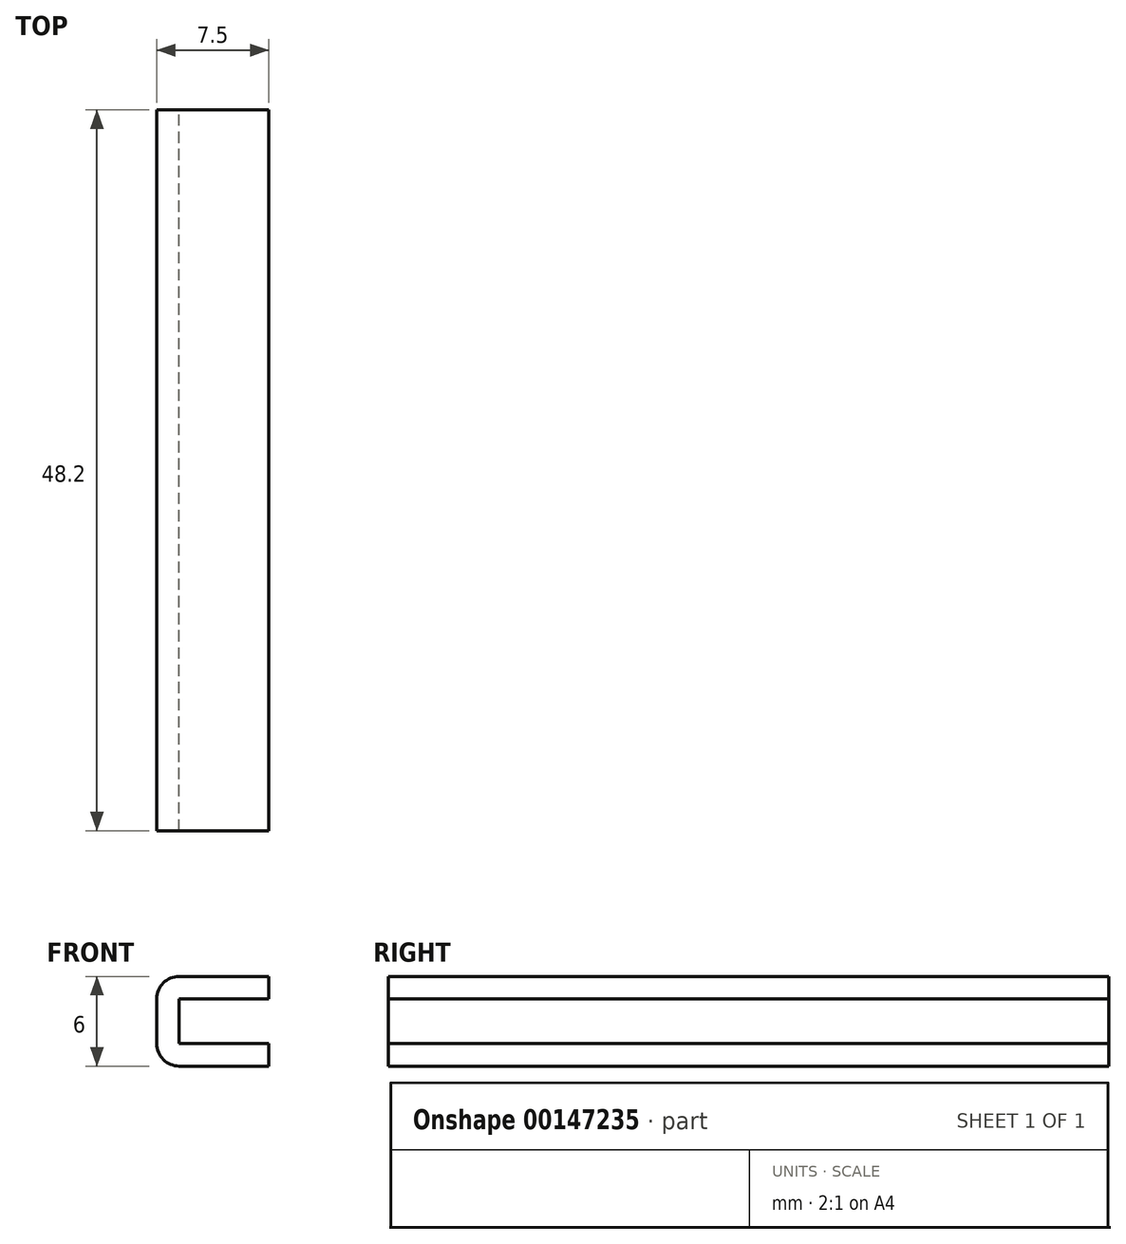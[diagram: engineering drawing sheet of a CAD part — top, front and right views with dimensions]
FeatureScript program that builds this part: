
annotation { "Feature Type Name" : "Feature", "Feature Type Description" : "" }
export const myFeature = defineFeature(function(context is Context, id is Id, definition is map)
    precondition{}
    {
        {
            var Q0;
            Q0=qCreatedBy(makeId("Front.planeOp"),FACE);
            var sketch = newSketch(context, id + "F0", { "sketchPlane" : qUnion([Q0])});
            skLineSegment(sketch, "E0", {"start": v(6, 1.5) * mm, "end": v(0, 1.5) * mm});
            skLineSegment(sketch, "E1", {"start": v(0, 1.5) * mm, "end": v(0, -1.5) * mm});
            skLineSegment(sketch, "E2", {"start": v(0, -1.5) * mm, "end": v(6, -1.5) * mm});
            skLineSegment(sketch, "E3", {"start": v(-1.5, 3) * mm, "end": v(6, 3) * mm});
            skLineSegment(sketch, "E4", {"start": v(6, 3) * mm, "end": v(6, 1.5) * mm});
            skLineSegment(sketch, "E5", {"start": v(6, -3) * mm, "end": v(-1.5, -3) * mm});
            skLineSegment(sketch, "E6.trimOffspring", {"start": v(6, -1.5) * mm, "end": v(6, -3) * mm});
            skLineSegment(sketch, "E7", {"start": v(-1.5, 3) * mm, "end": v(-1.5, -3) * mm});
            skSolve(sketch);
        }
        {
            var Q0;
            Q0 = qSketchRegion(id + "F0", true);
            extrude(context, id + "F1", {"entities" : qUnion([Q0]), "endBound" : BoundingType.SYMMETRIC, "depth" : 48.2 * mm});
        }
        {
            var Q0;
            Q0=makeQuery(id+"F1.opExtrude","SWEPT_EDGE",EDGE,{"disambiguationData":[OSD([sQuery(id+"F0.wireOp",EDGE,"E3"),sQuery(id+"F0.wireOp",EDGE,"E7")])]});
            var Q1;
            Q1=makeQuery(id+"F1.opExtrude","SWEPT_EDGE",EDGE,{"disambiguationData":[OSD([sQuery(id+"F0.wireOp",EDGE,"E5"),sQuery(id+"F0.wireOp",EDGE,"E7")])]});
            fillet(context, id + "F2", {"entities" : qUnion([Q0, Q1]), "radius" : 1.5 * mm, "tangentPropagation" : true, "allowEdgeOverflow" : false});
        }
    });
